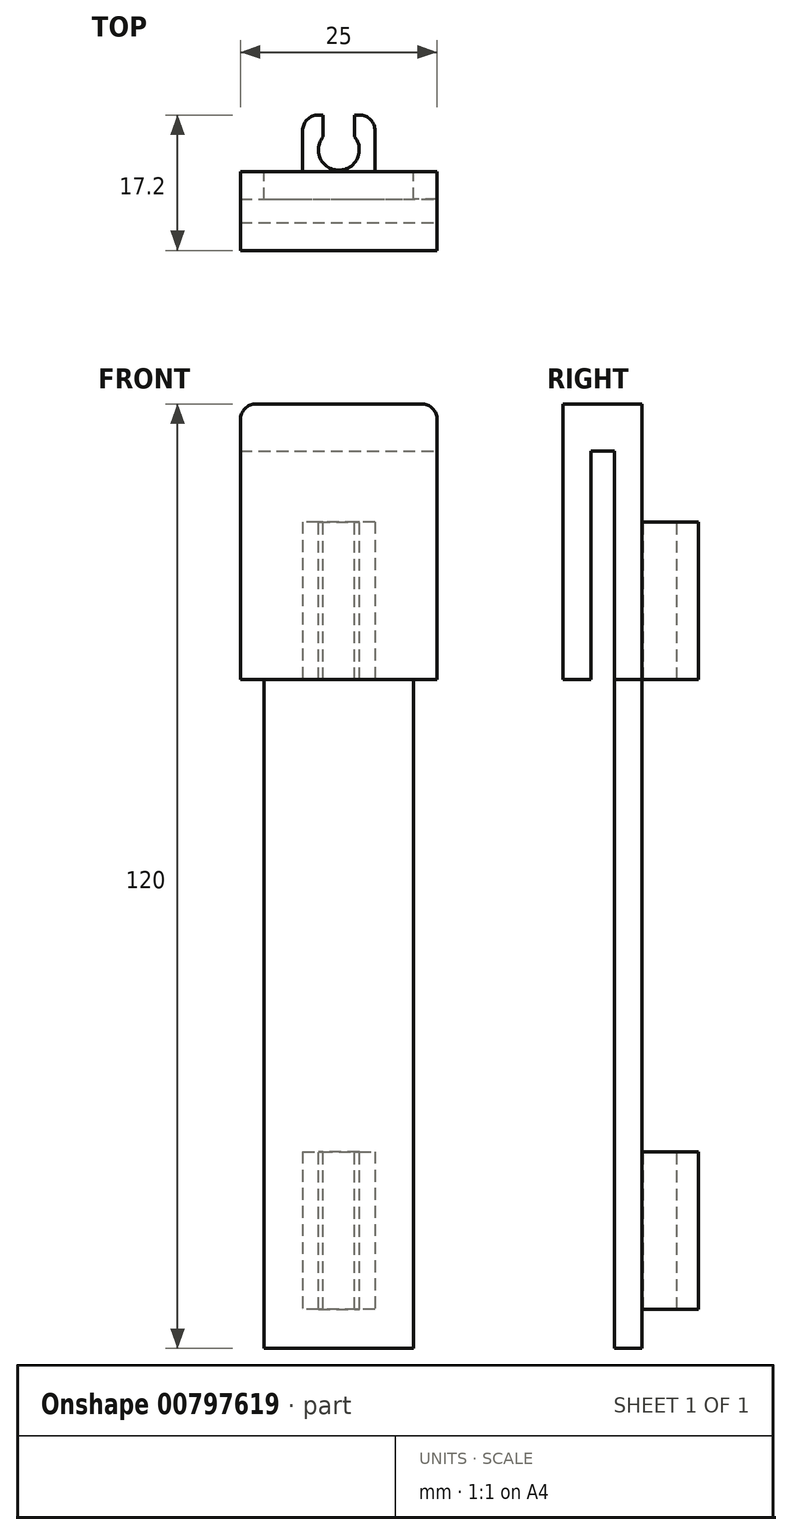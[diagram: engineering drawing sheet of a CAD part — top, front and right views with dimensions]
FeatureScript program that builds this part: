
annotation { "Feature Type Name" : "Feature", "Feature Type Description" : "" }
export const myFeature = defineFeature(function(context is Context, id is Id, definition is map)
    precondition{}
    {
        {
            var Q0;
            Q0=qCreatedBy(makeId("Front.planeOp"),FACE);
            var sketch = newSketch(context, id + "F0", { "sketchPlane" : qUnion([Q0])});
            skLineSegment(sketch, "E0.bottom", {"start": v(-12.5, -60) * mm, "end": v(12.5, -60) * mm});
            skLineSegment(sketch, "E0.top", {"start": v(-12.5, 60) * mm, "end": v(12.5, 60) * mm});
            skLineSegment(sketch, "E0.left", {"start": v(-12.5, -60) * mm, "end": v(-12.5, 60) * mm});
            skLineSegment(sketch, "E0.right", {"start": v(12.5, -60) * mm, "end": v(12.5, 60) * mm});
            skPoint(sketch, "E0.middle", {"position": v(0, 0) * mm});
            skSolve(sketch);
        }
        {
            var Q0;
            Q0=makeQuery(id+"F0.imprint","IMPRINT",FACE,{"disambiguationData":[TD([[makeQuery(id+"F0.imprint","IMPRINT",EDGE,{"derivedFrom":sQuery(id+"F0.wireOp",EDGE,"E0.bottom")}),1.0]])]});
            extrude(context, id + "F1", {"entities" : qUnion([Q0]), "depth" : 10 * mm, "offsetDistance" : 25 * mm});
        }
        {
            var Q0;
            Q0=makeQuery(id+"F1.opExtrude","SWEPT_FACE",FACE,{"disambiguationData":[OSD([sQuery(id+"F0.wireOp",EDGE,"E0.right")])]});
            var sketch = newSketch(context, id + "F2", { "sketchPlane" : qUnion([Q0])});
            skLineSegment(sketch, "E1", {"start": v(-5, 60) * mm, "end": v(-5, -72.57) * mm, "construction": true});
            skSolve(sketch);
        }
        {
            var Q0;
            {var subQ0=sQuery(id+"F0.wireOp",EDGE,"E0.right");Q0=makeQuery(id+"F2.imprint","IMPRINT",FACE,{"disambiguationData":[TD([[makeQuery(id+"F2.imprint","IMPRINT",EDGE,{"derivedFrom":makeQuery(id+"F1.opExtrude","CAP_EDGE",EDGE,{"disambiguationData":[OSD([subQ0])],"isStart":true})}),1.0]])]});}
            var sketch = newSketch(context, id + "F3", { "sketchPlane" : qUnion([Q0])});
            skLineSegment(sketch, "E2.bottom", {"start": v(-6.5, 54) * mm, "end": v(-3.5, 54) * mm});
            skLineSegment(sketch, "E2.top", {"start": v(-6.5, -60) * mm, "end": v(-3.5, -60) * mm});
            skLineSegment(sketch, "E2.left", {"start": v(-6.5, 54) * mm, "end": v(-6.5, -60) * mm});
            skLineSegment(sketch, "E2.right", {"start": v(-3.5, 54) * mm, "end": v(-3.5, -60) * mm});
            skSolve(sketch);
        }
        {
            var Q0;
            Q0 = qSketchRegion(id + "F3", true);
            extrude(context, id + "F4", {"entities" : qUnion([Q0]), "operationType" : NewBodyOperationType.REMOVE, "endBound" : BoundingType.THROUGH_ALL, "oppositeDirection" : true, "depth" : 25 * mm, "offsetDistance" : 25 * mm});
        }
        {
            var Q0;
            Q0=makeQuery(id+"F1.opExtrude","CAP_FACE",FACE,{"disambiguationData":[OSD([sQuery(id+"F0.wireOp",EDGE,"E0.bottom"),sQuery(id+"F0.wireOp",EDGE,"E0.top"),sQuery(id+"F0.wireOp",EDGE,"E0.left"),sQuery(id+"F0.wireOp",EDGE,"E0.right")])],"isStart":true});
            var sketch = newSketch(context, id + "F5", { "sketchPlane" : qUnion([Q0])});
            skLineSegment(sketch, "E3.bottom", {"start": v(-4.6, 45) * mm, "end": v(4.6, 45) * mm});
            skLineSegment(sketch, "E3.top", {"start": v(-4.6, -55) * mm, "end": v(4.6, -55) * mm});
            skLineSegment(sketch, "E3.left", {"start": v(-4.6, 45) * mm, "end": v(-4.6, -55) * mm});
            skLineSegment(sketch, "E3.right", {"start": v(4.6, 45) * mm, "end": v(4.6, -55) * mm});
            skSolve(sketch);
        }
        {
            var Q0;
            Q0=makeQuery(id+"F5.imprint","IMPRINT",FACE,{"disambiguationData":[TD([[makeQuery(id+"F5.imprint","IMPRINT",EDGE,{"derivedFrom":sQuery(id+"F5.wireOp",EDGE,"E3.bottom")}),-1.0]])]});
            extrude(context, id + "F6", {"entities" : qUnion([Q0]), "operationType" : NewBodyOperationType.ADD, "depth" : 7.2 * mm, "offsetDistance" : 25 * mm});
        }
        {
            var Q0;
            Q0=makeQuery(id+"F6.opExtrude","SWEPT_FACE",FACE,{"disambiguationData":[OSD([sQuery(id+"F5.wireOp",EDGE,"E3.bottom")])]});
            var sketch = newSketch(context, id + "F7", { "sketchPlane" : qUnion([Q0])});
            skCircle(sketch, "E4", {"center": v(0, 2.79) * mm, "radius": 2.6 * mm});
            skPoint(sketch, "E4.centerSnap0", {"position": v(0, 7.2) * mm});
            skSolve(sketch);
        }
        {
            var Q0;
            Q0=makeQuery(id+"F7.imprint","IMPRINT",FACE,{"disambiguationData":[TD([[makeQuery(id+"F7.imprint","IMPRINT",EDGE,{"derivedFrom":sQuery(id+"F7.wireOp",EDGE,"E4")}),1.0]])]});
            extrude(context, id + "F8", {"entities" : qUnion([Q0]), "operationType" : NewBodyOperationType.REMOVE, "endBound" : BoundingType.THROUGH_ALL, "oppositeDirection" : true, "depth" : 25 * mm, "offsetDistance" : 25 * mm});
        }
        {
            var Q0;
            Q0=makeQuery(id+"F6.opExtrude","CAP_FACE",FACE,{"disambiguationData":[OSD([sQuery(id+"F5.wireOp",EDGE,"E3.bottom"),sQuery(id+"F5.wireOp",EDGE,"E3.top"),sQuery(id+"F5.wireOp",EDGE,"E3.left"),sQuery(id+"F5.wireOp",EDGE,"E3.right")])],"isStart":false});
            var sketch = newSketch(context, id + "F9", { "sketchPlane" : qUnion([Q0])});
            skLineSegment(sketch, "E5.bottom", {"start": v(-2, -55) * mm, "end": v(2, -55) * mm});
            skLineSegment(sketch, "E5.top", {"start": v(-2, 45) * mm, "end": v(2, 45) * mm});
            skLineSegment(sketch, "E5.left", {"start": v(-2, -55) * mm, "end": v(-2, 45) * mm});
            skLineSegment(sketch, "E5.right", {"start": v(2, -55) * mm, "end": v(2, 45) * mm});
            skSolve(sketch);
        }
        {
            var Q0;
            Q0=makeQuery(id+"F9.imprint","IMPRINT",FACE,{"disambiguationData":[TD([[makeQuery(id+"F9.imprint","IMPRINT",EDGE,{"derivedFrom":sQuery(id+"F9.wireOp",EDGE,"E5.bottom")}),1.0]])]});
            extrude(context, id + "F10", {"entities" : qUnion([Q0]), "operationType" : NewBodyOperationType.REMOVE, "oppositeDirection" : true, "depth" : 3 * mm, "offsetDistance" : 25 * mm});
        }
        {
            var Q0;
            Q0=makeQuery(id+"F6.opExtrude","SWEPT_FACE",FACE,{"disambiguationData":[OSD([sQuery(id+"F5.wireOp",EDGE,"E3.left")])]});
            var sketch = newSketch(context, id + "F11", { "sketchPlane" : qUnion([Q0])});
            skLineSegment(sketch, "E6.bottom", {"start": v(0, 25) * mm, "end": v(7.2, 25) * mm});
            skLineSegment(sketch, "E6.top", {"start": v(0, -35) * mm, "end": v(7.2, -35) * mm});
            skLineSegment(sketch, "E6.left", {"start": v(0, 25) * mm, "end": v(0, -35) * mm});
            skLineSegment(sketch, "E6.right", {"start": v(7.2, 25) * mm, "end": v(7.2, -35) * mm});
            skSolve(sketch);
        }
        {
            var Q0;
            Q0=makeQuery(id+"F11.imprint","IMPRINT",FACE,{"disambiguationData":[TD([[makeQuery(id+"F11.imprint","IMPRINT",EDGE,{"derivedFrom":sQuery(id+"F11.wireOp",EDGE,"E6.bottom")}),-1.0]])]});
            extrude(context, id + "F12", {"entities" : qUnion([Q0]), "operationType" : NewBodyOperationType.REMOVE, "endBound" : BoundingType.THROUGH_ALL, "oppositeDirection" : true, "depth" : 25 * mm, "offsetDistance" : 25 * mm});
        }
        {
            var Q0;
            Q0=makeQuery(id+"F1.opExtrude","CAP_FACE",FACE,{"disambiguationData":[OSD([sQuery(id+"F0.wireOp",EDGE,"E0.bottom"),sQuery(id+"F0.wireOp",EDGE,"E0.top"),sQuery(id+"F0.wireOp",EDGE,"E0.left"),sQuery(id+"F0.wireOp",EDGE,"E0.right")])],"isStart":false});
            var sketch = newSketch(context, id + "F13", { "sketchPlane" : qUnion([Q0])});
            skLineSegment(sketch, "E7.bottom", {"start": v(-12.5, 25) * mm, "end": v(12.5, 25) * mm});
            skLineSegment(sketch, "E7.top", {"start": v(-12.5, -60) * mm, "end": v(12.5, -60) * mm});
            skLineSegment(sketch, "E7.left", {"start": v(-12.5, 25) * mm, "end": v(-12.5, -60) * mm});
            skLineSegment(sketch, "E7.right", {"start": v(12.5, 25) * mm, "end": v(12.5, -60) * mm});
            skSolve(sketch);
        }
        {
            var Q0;
            Q0=makeQuery(id+"F13.imprint","IMPRINT",FACE,{"disambiguationData":[TD([[makeQuery(id+"F13.imprint","IMPRINT",EDGE,{"derivedFrom":sQuery(id+"F13.wireOp",EDGE,"E7.bottom")}),-1.0]])]});
            extrude(context, id + "F14", {"entities" : qUnion([Q0]), "operationType" : NewBodyOperationType.REMOVE, "endBound" : BoundingType.UP_TO_NEXT, "oppositeDirection" : true, "depth" : 25 * mm, "offsetDistance" : 25 * mm});
        }
        {
            var Q0;
            Q0=makeQuery(id+"F12.boolean.opBoolean","MERGE",FACE,{"derivedFrom":[makeQuery(id+"F1.opExtrude","CAP_FACE",FACE,{"disambiguationData":[OSD([sQuery(id+"F0.wireOp",EDGE,"E0.bottom"),sQuery(id+"F0.wireOp",EDGE,"E0.top"),sQuery(id+"F0.wireOp",EDGE,"E0.left"),sQuery(id+"F0.wireOp",EDGE,"E0.right")])],"isStart":true}),makeQuery(id+"F12.opExtrude","SWEPT_FACE",FACE,{"disambiguationData":[OSD([sQuery(id+"F11.wireOp",EDGE,"E6.left")])]})]});
            var sketch = newSketch(context, id + "F15", { "sketchPlane" : qUnion([Q0])});
            skLineSegment(sketch, "E8.bottom", {"start": v(-12.5, 25) * mm, "end": v(-9.5, 25) * mm});
            skLineSegment(sketch, "E8.top", {"start": v(-12.5, -60) * mm, "end": v(-9.5, -60) * mm});
            skLineSegment(sketch, "E8.left", {"start": v(-12.5, 25) * mm, "end": v(-12.5, -60) * mm});
            skLineSegment(sketch, "E8.right", {"start": v(-9.5, 25) * mm, "end": v(-9.5, -60) * mm});
            skLineSegment(sketch, "E9.bottom", {"start": v(12.5, 25) * mm, "end": v(9.5, 25) * mm});
            skLineSegment(sketch, "E9.top", {"start": v(12.5, -60) * mm, "end": v(9.5, -60) * mm});
            skLineSegment(sketch, "E9.left", {"start": v(12.5, 25) * mm, "end": v(12.5, -60) * mm});
            skLineSegment(sketch, "E9.right", {"start": v(9.5, 25) * mm, "end": v(9.5, -60) * mm});
            skSolve(sketch);
        }
        {
            var Q0;
            Q0=makeQuery(id+"F15.imprint","IMPRINT",FACE,{"disambiguationData":[TD([[makeQuery(id+"F15.imprint","IMPRINT",EDGE,{"derivedFrom":sQuery(id+"F15.wireOp",EDGE,"E8.bottom")}),-1.0]])]});
            var Q1;
            Q1=makeQuery(id+"F15.imprint","IMPRINT",FACE,{"disambiguationData":[TD([[makeQuery(id+"F15.imprint","IMPRINT",EDGE,{"derivedFrom":sQuery(id+"F15.wireOp",EDGE,"E9.bottom")}),1.0]])]});
            extrude(context, id + "F16", {"entities" : qUnion([Q0, Q1]), "operationType" : NewBodyOperationType.REMOVE, "endBound" : BoundingType.UP_TO_NEXT, "oppositeDirection" : true, "depth" : 25 * mm, "offsetDistance" : 25 * mm});
        }
        {
            var Q0;
            Q0=makeQuery(id+"F14.boolean.opBoolean","COPY",EDGE,{"derivedFrom":makeQuery(id+"F14.opExtrude","SWEPT_EDGE",EDGE,{"disambiguationData":[OSD([sQuery(id+"F0.wireOp",EDGE,"E0.left"),sQuery(id+"F13.wireOp",EDGE,"E7.bottom"),sQuery(id+"F13.wireOp",EDGE,"E7.left")])]})});
            var Q1;
            Q1=makeQuery(id+"F16.boolean.opBoolean","COPY",EDGE,{"derivedFrom":makeQuery(id+"F16.opExtrude","SWEPT_EDGE",EDGE,{"disambiguationData":[OSD([sQuery(id+"F0.wireOp",EDGE,"E0.left"),sQuery(id+"F15.wireOp",EDGE,"E9.bottom"),sQuery(id+"F15.wireOp",EDGE,"E9.left")])]})});
            var Q2;
            Q2=makeQuery(id+"F16.boolean.opBoolean","COPY",EDGE,{"derivedFrom":makeQuery(id+"F16.opExtrude","SWEPT_EDGE",EDGE,{"disambiguationData":[OSD([sQuery(id+"F0.wireOp",EDGE,"E0.right"),sQuery(id+"F15.wireOp",EDGE,"E8.bottom"),sQuery(id+"F15.wireOp",EDGE,"E8.left")])]})});
            var Q3;
            Q3=makeQuery(id+"F14.boolean.opBoolean","COPY",EDGE,{"derivedFrom":makeQuery(id+"F14.opExtrude","SWEPT_EDGE",EDGE,{"disambiguationData":[OSD([sQuery(id+"F0.wireOp",EDGE,"E0.right"),sQuery(id+"F13.wireOp",EDGE,"E7.bottom"),sQuery(id+"F13.wireOp",EDGE,"E7.right")])]})});
            var Q4;
            Q4=makeQuery(id+"F1.opExtrude","SWEPT_EDGE",EDGE,{"disambiguationData":[OSD([sQuery(id+"F0.wireOp",EDGE,"E0.top"),sQuery(id+"F0.wireOp",EDGE,"E0.left")])]});
            var Q5;
            Q5=makeQuery(id+"F1.opExtrude","SWEPT_EDGE",EDGE,{"disambiguationData":[OSD([sQuery(id+"F0.wireOp",EDGE,"E0.top"),sQuery(id+"F0.wireOp",EDGE,"E0.right")])]});
            var Q6;
            Q6=makeQuery(id+"F16.boolean.opBoolean","COPY",EDGE,{"derivedFrom":makeQuery(id+"F16.opExtrude","SWEPT_EDGE",EDGE,{"disambiguationData":[OSD([sQuery(id+"F0.wireOp",EDGE,"E0.bottom"),sQuery(id+"F15.wireOp",EDGE,"E9.top"),sQuery(id+"F15.wireOp",EDGE,"E9.right")])]})});
            var Q7;
            Q7=makeQuery(id+"F16.boolean.opBoolean","COPY",EDGE,{"derivedFrom":makeQuery(id+"F16.opExtrude","SWEPT_EDGE",EDGE,{"disambiguationData":[OSD([sQuery(id+"F0.wireOp",EDGE,"E0.bottom"),sQuery(id+"F15.wireOp",EDGE,"E8.top"),sQuery(id+"F15.wireOp",EDGE,"E8.right")])]})});
            var Q8;
            {var subQ0=sQuery(id+"F5.wireOp",EDGE,"E3.bottom");var subQ1=sQuery(id+"F5.wireOp",EDGE,"E3.right");Q8=makeQuery(id+"F12.boolean.opBoolean","SPLIT",EDGE,{"disambiguationData":[TD([makeQuery(id+"F6.opExtrude","SWEPT_FACE",FACE,{"disambiguationData":[OSD([subQ0])]})])],"derivedFrom":makeQuery(id+"F6.opExtrude","CAP_EDGE",EDGE,{"disambiguationData":[OSD([subQ1])],"isStart":false})});}
            var Q9;
            {var subQ0=sQuery(id+"F5.wireOp",EDGE,"E3.bottom");var subQ1=sQuery(id+"F5.wireOp",EDGE,"E3.left");Q9=makeQuery(id+"F12.boolean.opBoolean","SPLIT",EDGE,{"disambiguationData":[TD([makeQuery(id+"F6.opExtrude","SWEPT_FACE",FACE,{"disambiguationData":[OSD([subQ0])]})])],"derivedFrom":makeQuery(id+"F6.opExtrude","CAP_EDGE",EDGE,{"disambiguationData":[OSD([subQ1])],"isStart":false})});}
            var Q10;
            {var subQ0=sQuery(id+"F5.wireOp",EDGE,"E3.right");Q10=makeQuery(id+"F12.boolean.opBoolean","SPLIT",EDGE,{"disambiguationData":[TD([makeQuery(id+"F6.opExtrude","SWEPT_FACE",FACE,{"disambiguationData":[OSD([sQuery(id+"F5.wireOp",EDGE,"E3.bottom")])]})])],"derivedFrom":makeQuery(id+"F6.opExtrude","CAP_EDGE",EDGE,{"disambiguationData":[OSD([subQ0])],"isStart":true})});}
            var Q11;
            {var subQ0=sQuery(id+"F5.wireOp",EDGE,"E3.left");Q11=makeQuery(id+"F12.boolean.opBoolean","SPLIT",EDGE,{"disambiguationData":[TD([makeQuery(id+"F6.opExtrude","SWEPT_FACE",FACE,{"disambiguationData":[OSD([sQuery(id+"F5.wireOp",EDGE,"E3.bottom")])]})])],"derivedFrom":makeQuery(id+"F6.opExtrude","CAP_EDGE",EDGE,{"disambiguationData":[OSD([subQ0])],"isStart":true})});}
            var Q12;
            {var subQ0=sQuery(id+"F5.wireOp",EDGE,"E3.right");var subQ1=sQuery(id+"F5.wireOp",EDGE,"E3.top");Q12=makeQuery(id+"F12.boolean.opBoolean","SPLIT",EDGE,{"disambiguationData":[TD([makeQuery(id+"F6.opExtrude","SWEPT_FACE",FACE,{"disambiguationData":[OSD([subQ1])]})])],"derivedFrom":makeQuery(id+"F6.opExtrude","CAP_EDGE",EDGE,{"disambiguationData":[OSD([subQ0])],"isStart":false})});}
            var Q13;
            {var subQ0=sQuery(id+"F5.wireOp",EDGE,"E3.left");var subQ1=sQuery(id+"F5.wireOp",EDGE,"E3.top");Q13=makeQuery(id+"F12.boolean.opBoolean","SPLIT",EDGE,{"disambiguationData":[TD([makeQuery(id+"F6.opExtrude","SWEPT_FACE",FACE,{"disambiguationData":[OSD([subQ1])]})])],"derivedFrom":makeQuery(id+"F6.opExtrude","CAP_EDGE",EDGE,{"disambiguationData":[OSD([subQ0])],"isStart":false})});}
            var Q14;
            {var subQ0=sQuery(id+"F5.wireOp",EDGE,"E3.right");Q14=makeQuery(id+"F12.boolean.opBoolean","SPLIT",EDGE,{"disambiguationData":[TD([makeQuery(id+"F6.opExtrude","SWEPT_FACE",FACE,{"disambiguationData":[OSD([sQuery(id+"F5.wireOp",EDGE,"E3.top")])]})])],"derivedFrom":makeQuery(id+"F6.opExtrude","CAP_EDGE",EDGE,{"disambiguationData":[OSD([subQ0])],"isStart":true})});}
            var Q15;
            {var subQ0=sQuery(id+"F5.wireOp",EDGE,"E3.left");Q15=makeQuery(id+"F12.boolean.opBoolean","SPLIT",EDGE,{"disambiguationData":[TD([makeQuery(id+"F6.opExtrude","SWEPT_FACE",FACE,{"disambiguationData":[OSD([sQuery(id+"F5.wireOp",EDGE,"E3.top")])]})])],"derivedFrom":makeQuery(id+"F6.opExtrude","CAP_EDGE",EDGE,{"disambiguationData":[OSD([subQ0])],"isStart":true})});}
            fillet(context, id + "F17", {"entities" : qUnion([Q0, Q1, Q2, Q3, Q4, Q5, Q6, Q7, Q8, Q9, Q10, Q11, Q12, Q13, Q14, Q15]), "radius" : 2 * mm, "tangentPropagation" : true, "allowEdgeOverflow" : false});
        }
    });
